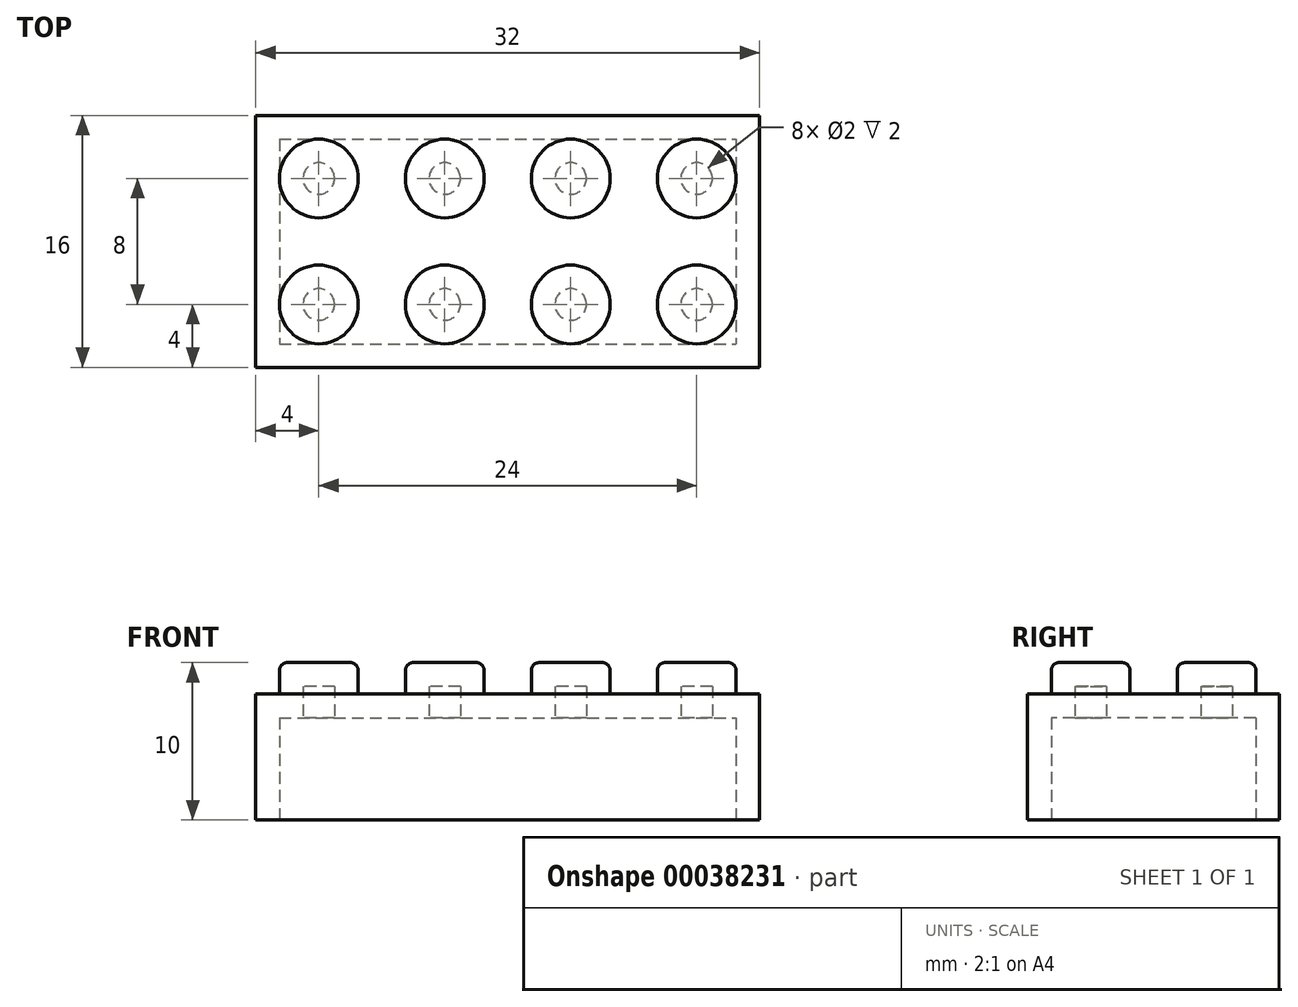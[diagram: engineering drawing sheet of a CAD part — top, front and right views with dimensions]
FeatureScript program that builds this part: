
annotation { "Feature Type Name" : "Feature", "Feature Type Description" : "" }
export const myFeature = defineFeature(function(context is Context, id is Id, definition is map)
    precondition{}
    {
        {
            var Q0;
            Q0=qCreatedBy(makeId("Top.planeOp"),FACE);
            var sketch = newSketch(context, id + "F0", { "sketchPlane" : qUnion([Q0])});
            skLineSegment(sketch, "E0.rect.bottom", {"start": v(-16, 8) * mm, "end": v(16, 8) * mm});
            skLineSegment(sketch, "E0.rect.top", {"start": v(-16, -8) * mm, "end": v(16, -8) * mm});
            skLineSegment(sketch, "E0.rect.left", {"start": v(-16, 8) * mm, "end": v(-16, -8) * mm});
            skLineSegment(sketch, "E0.rect.right", {"start": v(16, 8) * mm, "end": v(16, -8) * mm});
            skPoint(sketch, "E0.rect.middle", {"position": v(0, 0) * mm});
            skSolve(sketch);
        }
        {
            var Q0;
            Q0=qCreatedBy(makeId("Top.planeOp"),FACE);
            var Q1;
            Q1 = qBodyType(qCreatedBy(id + "FS5KcXyeSzJ0Lcl_1" ,EDGE), BodyType.WIRE);
            cPlane(context, id + "F1", {"entities" : qUnion([Q0, Q1]), "cplaneType" : CPlaneType.OFFSET, "offset" : 8 * mm, "width" : 150 * mm, "height" : 150 * mm});
        }
        {
            var Q0;
            Q0=makeQuery(id+"F0.imprint","IMPRINT",FACE,{"disambiguationData":[TD([[makeQuery(id+"F0.imprint","IMPRINT",EDGE,{"derivedFrom":sQuery(id+"F0.wireOp",EDGE,"E0.rect.bottom")}),-1.0]])]});
            extrude(context, id + "F2", {"entities" : qUnion([Q0]), "depth" : 8 * mm});
        }
        {
            var Q0;
            Q0=qCreatedBy(id+"F1.planeOp",FACE);
            var sketch = newSketch(context, id + "F3", { "sketchPlane" : qUnion([Q0])});
            skLineSegment(sketch, "E1.rect.bottom", {"start": v(-16, 8) * mm, "end": v(16, 8) * mm, "construction": true});
            skLineSegment(sketch, "E1.rect.top", {"start": v(-16, -8) * mm, "end": v(16, -8) * mm, "construction": true});
            skLineSegment(sketch, "E1.rect.left", {"start": v(-16, 8) * mm, "end": v(-16, -8) * mm, "construction": true});
            skLineSegment(sketch, "E1.rect.right", {"start": v(16, 8) * mm, "end": v(16, -8) * mm, "construction": true});
            skPoint(sketch, "E1.rect.middle", {"position": v(0, 0) * mm});
            skLineSegment(sketch, "E2", {"start": v(-16, 8) * mm, "end": v(-12, 8) * mm, "construction": true});
            skLineSegment(sketch, "E3", {"start": v(-16, 8) * mm, "end": v(-16, 4) * mm, "construction": true});
            skLineSegment(sketch, "E4", {"start": v(-12, 8) * mm, "end": v(-4, 8) * mm, "construction": true});
            skLineSegment(sketch, "E5", {"start": v(-4, 8) * mm, "end": v(4, 8) * mm});
            skLineSegment(sketch, "E6", {"start": v(4, 8) * mm, "end": v(12, 8) * mm, "construction": true});
            skLineSegment(sketch, "E7", {"start": v(12, 8) * mm, "end": v(16, 8) * mm, "construction": true});
            skLineSegment(sketch, "E8", {"start": v(-16, 4) * mm, "end": v(-16, 0) * mm, "construction": true});
            skLineSegment(sketch, "E9", {"start": v(-16, 4) * mm, "end": v(16, 4) * mm, "construction": true});
            skLineSegment(sketch, "E10", {"start": v(16, 4) * mm, "end": v(16, 8) * mm, "construction": true});
            skLineSegment(sketch, "E11", {"start": v(-16, 0) * mm, "end": v(16, 0) * mm, "construction": true});
            skLineSegment(sketch, "E12", {"start": v(-12, 8) * mm, "end": v(-12, 0) * mm, "construction": true});
            skLineSegment(sketch, "E13", {"start": v(-4, 8) * mm, "end": v(-4, 0) * mm, "construction": true});
            skLineSegment(sketch, "E14", {"start": v(4, 8) * mm, "end": v(4, 0) * mm, "construction": true});
            skLineSegment(sketch, "E15", {"start": v(12, 8) * mm, "end": v(12, 0) * mm, "construction": true});
            skCircle(sketch, "E16", {"center": v(-12, 4) * mm, "radius": 2.5 * mm});
            skLineSegment(sketch, "E17", {"start": v(-4, 8) * mm, "end": v(-4, 4) * mm, "construction": true});
            skLineSegment(sketch, "E18", {"start": v(4, 8) * mm, "end": v(4, 4) * mm, "construction": true});
            skLineSegment(sketch, "E19", {"start": v(12, 8) * mm, "end": v(12, 4) * mm, "construction": true});
            skCircle(sketch, "E20", {"center": v(-4, 4) * mm, "radius": 2.5 * mm});
            skCircle(sketch, "E21", {"center": v(4, 4) * mm, "radius": 2.5 * mm});
            skCircle(sketch, "E22", {"center": v(12, 4) * mm, "radius": 2.5 * mm});
            skCircle(sketch, "E23.MirrorC", {"center": v(4, -4) * mm, "radius": 2.5 * mm});
            skCircle(sketch, "E24.MirrorC", {"center": v(-4, -4) * mm, "radius": 2.5 * mm});
            skCircle(sketch, "E25.MirrorC", {"center": v(-12, -4) * mm, "radius": 2.5 * mm});
            skCircle(sketch, "E26.MirrorC", {"center": v(12, -4) * mm, "radius": 2.5 * mm});
            skSolve(sketch);
        }
        {
            var Q0;
            Q0 = qSketchRegion(id + "F3", true);
            var Q1;
            Q1=makeQuery(id+"F3.imprint","IMPRINT",FACE,{"disambiguationData":[TD([[makeQuery(id+"F3.imprint","IMPRINT",EDGE,{"derivedFrom":sQuery(id+"F3.wireOp",EDGE,"E16")}),1.0]])]});
            extrude(context, id + "F4", {"entities" : qUnion([Q0, Q1]), "operationType" : NewBodyOperationType.ADD, "depth" : 2 * mm});
        }
        {
            var Q0;
            Q0=makeQuery(id+"F4.opExtrude","CAP_EDGE",EDGE,{"disambiguationData":[OSD([sQuery(id+"F3.wireOp",EDGE,"E16")])],"isStart":false});
            var Q1;
            Q1=makeQuery(id+"F4.opExtrude","CAP_EDGE",EDGE,{"disambiguationData":[OSD([sQuery(id+"F3.wireOp",EDGE,"E20")])],"isStart":false});
            var Q2;
            Q2=makeQuery(id+"F4.opExtrude","CAP_EDGE",EDGE,{"disambiguationData":[OSD([sQuery(id+"F3.wireOp",EDGE,"E21")])],"isStart":false});
            var Q3;
            Q3=makeQuery(id+"F4.opExtrude","CAP_EDGE",EDGE,{"disambiguationData":[OSD([sQuery(id+"F3.wireOp",EDGE,"E22")])],"isStart":false});
            var Q4;
            Q4=makeQuery(id+"F4.opExtrude","CAP_EDGE",EDGE,{"disambiguationData":[OSD([sQuery(id+"F3.wireOp",EDGE,"E26.MirrorC")])],"isStart":false});
            var Q5;
            Q5=makeQuery(id+"F4.opExtrude","CAP_EDGE",EDGE,{"disambiguationData":[OSD([sQuery(id+"F3.wireOp",EDGE,"E23.MirrorC")])],"isStart":false});
            var Q6;
            Q6=makeQuery(id+"F4.opExtrude","CAP_EDGE",EDGE,{"disambiguationData":[OSD([sQuery(id+"F3.wireOp",EDGE,"E24.MirrorC")])],"isStart":false});
            var Q7;
            Q7=makeQuery(id+"F4.opExtrude","CAP_EDGE",EDGE,{"disambiguationData":[OSD([sQuery(id+"F3.wireOp",EDGE,"E25.MirrorC")])],"isStart":false});
            fillet(context, id + "F5", {"entities" : qUnion([Q0, Q1, Q2, Q3, Q4, Q5, Q6, Q7]), "radius" : 0.5 * mm, "tangentPropagation" : true, "allowEdgeOverflow" : false});
        }
        {
            var Q0;
            Q0=qCreatedBy(makeId("Top.planeOp"),FACE);
            cPlane(context, id + "F6", {"entities" : qUnion([Q0]), "cplaneType" : CPlaneType.OFFSET, "offset" : 0 * mm, "width" : 150 * mm, "height" : 150 * mm});
        }
        {
            var Q0;
            Q0=qCreatedBy(id+"F6.planeOp",FACE);
            var sketch = newSketch(context, id + "F7", { "sketchPlane" : qUnion([Q0])});
            skLineSegment(sketch, "E27.rect.bottom", {"start": v(-16, -8) * mm, "end": v(16, -8) * mm});
            skLineSegment(sketch, "E27.rect.top", {"start": v(-16, 8) * mm, "end": v(16, 8) * mm});
            skLineSegment(sketch, "E27.rect.left", {"start": v(-16, -8) * mm, "end": v(-16, 8) * mm});
            skLineSegment(sketch, "E27.rect.right", {"start": v(16, -8) * mm, "end": v(16, 8) * mm});
            skPoint(sketch, "E27.rect.middle", {"position": v(0, 0) * mm});
            skLineSegment(sketch, "E28", {"start": v(-16, -8) * mm, "end": v(-8, -8) * mm, "construction": true});
            skLineSegment(sketch, "E29", {"start": v(-8, -8) * mm, "end": v(0, -8) * mm, "construction": true});
            skLineSegment(sketch, "E30", {"start": v(0, -8) * mm, "end": v(8, -8) * mm, "construction": true});
            skLineSegment(sketch, "E31", {"start": v(8, -8) * mm, "end": v(16, -8) * mm, "construction": true});
            skLineSegment(sketch, "E32", {"start": v(-8, -8) * mm, "end": v(-8, 8) * mm, "construction": true});
            skLineSegment(sketch, "E33", {"start": v(0, -8) * mm, "end": v(0, 8) * mm, "construction": true});
            skLineSegment(sketch, "E34", {"start": v(8, -8) * mm, "end": v(8, 8) * mm, "construction": true});
            skLineSegment(sketch, "E35", {"start": v(-16, 0) * mm, "end": v(16, 0) * mm, "construction": true});
            skCircle(sketch, "E36", {"center": v(-8, 0) * mm, "radius": 3.58 * mm});
            skCircle(sketch, "E37", {"center": v(0, 0) * mm, "radius": 3.58 * mm});
            skCircle(sketch, "E38", {"center": v(8, 0) * mm, "radius": 3.58 * mm});
            skSolve(sketch);
        }
        {
            var Q0;
            Q0=makeQuery(id+"F7.imprint","IMPRINT",FACE,{"disambiguationData":[TD([[makeQuery(id+"F7.imprint","IMPRINT",EDGE,{"derivedFrom":sQuery(id+"F7.wireOp",EDGE,"E36")}),1.0]])]});
            var Q1;
            Q1=makeQuery(id+"F7.imprint","IMPRINT",FACE,{"disambiguationData":[TD([[makeQuery(id+"F7.imprint","IMPRINT",EDGE,{"derivedFrom":sQuery(id+"F7.wireOp",EDGE,"E37")}),1.0]])]});
            var Q2;
            Q2=makeQuery(id+"F7.imprint","IMPRINT",FACE,{"disambiguationData":[TD([[makeQuery(id+"F7.imprint","IMPRINT",EDGE,{"derivedFrom":sQuery(id+"F7.wireOp",EDGE,"E38")}),1.0]])]});
            extrude(context, id + "F8", {"entities" : qUnion([Q0, Q1, Q2]), "operationType" : NewBodyOperationType.ADD, "depth" : 8 * mm});
        }
        {
            var Q0;
            Q0=makeQuery(id+"F2.opExtrude","CAP_FACE",FACE,{"disambiguationData":[OSD([sQuery(id+"F0.wireOp",EDGE,"E0.rect.bottom"),sQuery(id+"F0.wireOp",EDGE,"E0.rect.top"),sQuery(id+"F0.wireOp",EDGE,"E0.rect.left"),sQuery(id+"F0.wireOp",EDGE,"E0.rect.right")])],"isStart":true});
            shell(context, id + "F9", {"entities" : qUnion([Q0]), "thickness" : 1.5 * mm});
        }
    });
